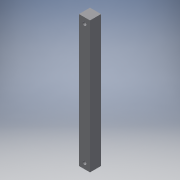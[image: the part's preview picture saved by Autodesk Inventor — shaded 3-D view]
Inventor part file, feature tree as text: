
AUTODESK INVENTOR PART (.ipt)
format: ipt  version: 2018 (Build 220112000, 112)  size: 102,400 bytes
history: native  units: mm
features: sketch x2, extrude x1, hole x1
ambient origin geometry x8: Origin, YZ Plane, XZ Plane, XY Plane, X Axis, Y Axis, Z Axis, Center Point
bodies: Body1 (feature_tree)
feature tree (4):
  extrude  "押し出し2"  Depth=30.0mm
  hole  "穴2"  [1 undecoded]
  sketch  "スケッチ4"
  sketch  "スケッチ5"
note: 1 required parameter value undecoded (feature->parameter linkage not recoverable at this tier; creation-order binding heuristic only, values carry confidence <= 0.55)
